# Revit family: Tube with parameters write family
name_source: partatom
category: Generic Models
units: mm (PartAtom-declared; Revit-internal decimal feet)

## family parameters
Always vertical = No
Can host rebar = No
Cut with Voids When Loaded = No
Part Type = Normal
Room Calculation Point = No
Round Connector Dimension = Use Diameter
Shared = Yes
Work Plane-Based = No

## types (1)
- Tube with parameters write family
    Ankerlengte (mm) = 0 mm  [stored 0 ft]
    Breedte = 0 mm  [stored 0 ft]
    Default Elevation = 0 mm  [stored 0 ft]
    Dikte (mm) = 0 mm  [stored 0 ft]
    Geluidsabsorbtiewaarde (dB) = 0
    Geluidsisolatie (dB) = 0
    Hoogte = 0 mm  [stored 0 ft]
    Hoogte betonprop (mm) = 0 mm  [stored 0 ft]
    Lengte = 0 mm  [stored 0 ft]
    Levensduur (jaar) = 0
    Ondersabelingsdikte (mm) = 0 mm  [stored 0 ft]

note: [stored X ft] marks values corroborated as IEEE doubles in the binary element streams (Revit-internal decimal feet)

## geometry (parser evidence)
native form markers: Sweep x4
no freeform markers — native parametric forms only
